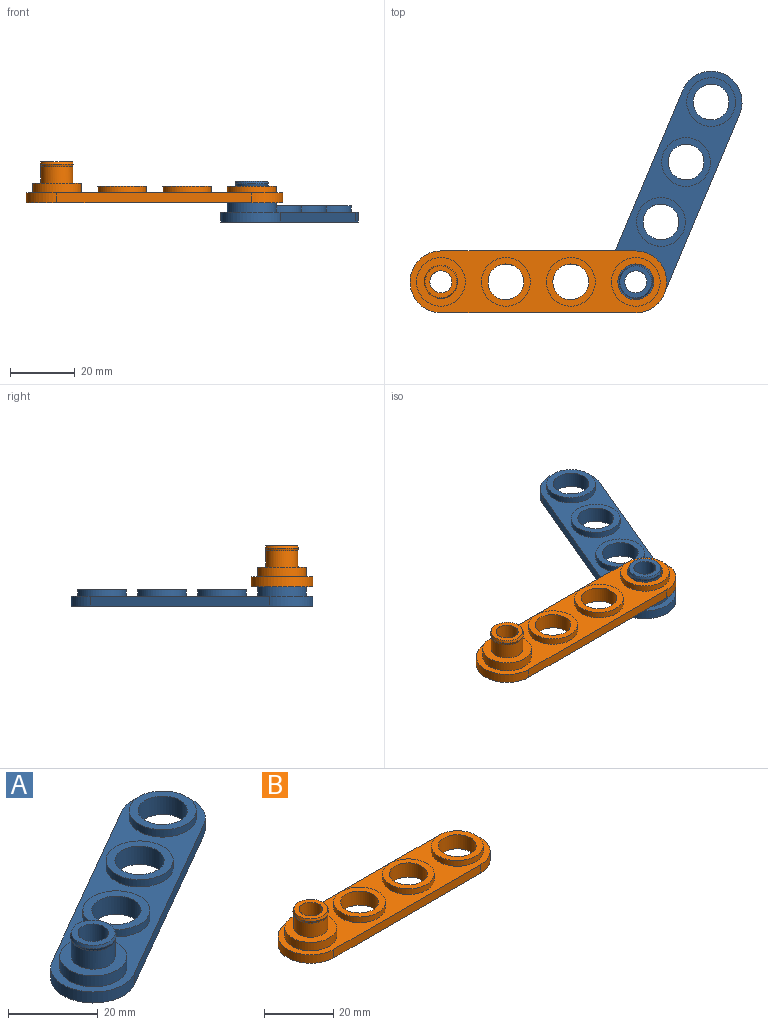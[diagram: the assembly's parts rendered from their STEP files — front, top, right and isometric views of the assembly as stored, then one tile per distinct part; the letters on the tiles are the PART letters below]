
ASSEMBLY  parts=2 mates=1
PART A: 22 faces, bbox 71x49x12.5 mm
  f0: cylinder r=9.5mm len=17.73mm, axis (0,0,-1), area 89.5mm2, adj f1,f3,f4,f5
  f1: plane 51.96x30mm, normal (0.5,-0.87,0), area 180mm2, adj f0,f2,f4,f5
  f2: cylinder r=9.5mm len=17.73mm, axis (0,0,-1), area 89.5mm2, adj f1,f3,f4,f5
  f3: plane 51.96x30mm, normal (-0.5,0.87,0), area 180mm2, adj f0,f2,f4,f5
  f4: plane 70.96x49mm, normal (0,0,1), area 716.7mm2, adj f0,f1,f2,f3,f6,f9,f12,f15
  f5: plane 70.96x49mm, normal (0,0,-1), area 1102.1mm2, adj f0,f1,f2,f3,f7,f10,f13,f18
  f6: cylinder r=7.5mm len=15mm, axis (0,0,-1), area 94.2mm2, adj f4,f8
  f7: cylinder r=5.5mm len=11mm, axis (0,0,-1), area 172.8mm2, adj f5,f8
  f8: plane 15x15mm, normal (0,0,1), area 81.7mm2, adj f6,f7
  f9: cylinder r=7.5mm len=15mm, axis (0,0,-1), area 94.2mm2, adj f4,f11
  f10: cylinder r=5.5mm len=11mm, axis (0,0,-1), area 172.8mm2, adj f5,f11
  f11: plane 15x15mm, normal (0,0,1), area 81.7mm2, adj f9,f10
  f12: cylinder r=7.5mm len=15mm, axis (0,0,-1), area 94.2mm2, adj f4,f14
  f13: cylinder r=5.5mm len=11mm, axis (0,0,-1), area 172.8mm2, adj f5,f14
  f14: plane 15x15mm, normal (0,0,1), area 81.7mm2, adj f12,f13
  f15: cylinder r=7.5mm len=15mm, axis (0,0,-1), area 141.4mm2, adj f4,f16
  f16: plane 15x15mm, normal (0,0,1), area 101.3mm2, adj f15,f17
  f17: cylinder r=4.9mm len=9.8mm, axis (0,0,-1), area 153.9mm2, adj f16,f21
  f18: cylinder r=3.4mm len=12.5mm, axis (0,0,-1), area 267mm2, adj f5,f19
  f19: plane 9.8x9.8mm, normal (0,0,1), area 39.1mm2, adj f18,f20
  f20: cone r=4.9mm half-angle=18.4deg, axis (0,0,-1), area 25mm2, adj f19,f21
  f21: cone r=5.15mm half-angle=18.4deg, axis (0,0,1), area 25mm2, adj f17,f20
PART B: 22 faces, bbox 79x19x12.5 mm
  f0: cylinder r=9.5mm len=19mm, axis (0,0,-1), area 89.5mm2, adj f1,f3,f4,f5
  f1: plane 60x3mm, normal (0,-1,0), area 180mm2, adj f0,f2,f4,f5
  f2: cylinder r=9.5mm len=19mm, axis (0,0,-1), area 89.5mm2, adj f1,f3,f4,f5
  f3: plane 60x3mm, normal (0,1,0), area 180mm2, adj f0,f2,f4,f5
  f4: plane 79x19mm, normal (0,0,1), area 716.7mm2, adj f0,f1,f2,f3,f6,f9,f12,f15
  f5: plane 79x19mm, normal (0,0,-1), area 1102.1mm2, adj f0,f1,f2,f3,f7,f10,f13,f18
  f6: cylinder r=7.5mm len=15mm, axis (0,0,-1), area 94.2mm2, adj f4,f8
  f7: cylinder r=5.5mm len=11mm, axis (0,0,-1), area 172.8mm2, adj f5,f8
  f8: plane 15x15mm, normal (0,0,1), area 81.7mm2, adj f6,f7
  f9: cylinder r=7.5mm len=15mm, axis (0,0,-1), area 94.2mm2, adj f4,f11
  f10: cylinder r=5.5mm len=11mm, axis (0,0,-1), area 172.8mm2, adj f5,f11
  f11: plane 15x15mm, normal (0,0,1), area 81.7mm2, adj f9,f10
  f12: cylinder r=7.5mm len=15mm, axis (0,0,-1), area 94.2mm2, adj f4,f14
  f13: cylinder r=5.5mm len=11mm, axis (0,0,-1), area 172.8mm2, adj f5,f14
  f14: plane 15x15mm, normal (0,0,1), area 81.7mm2, adj f12,f13
  f15: cylinder r=7.5mm len=15mm, axis (0,0,-1), area 141.4mm2, adj f4,f16
  f16: plane 15x15mm, normal (0,0,1), area 101.3mm2, adj f15,f17
  f17: cylinder r=4.9mm len=9.8mm, axis (0,0,-1), area 153.9mm2, adj f16,f21
  f18: cylinder r=3.4mm len=12.5mm, axis (0,0,-1), area 267mm2, adj f5,f19
  f19: plane 9.8x9.8mm, normal (0,0,1), area 39.1mm2, adj f18,f20
  f20: cone r=4.9mm half-angle=18.4deg, axis (0,0,-1), area 25mm2, adj f19,f21
  f21: cone r=5.15mm half-angle=18.4deg, axis (0,0,1), area 25mm2, adj f17,f20
PLACE A rot(axis=(0,0,1),37.3deg) t=(12.14,-36.73,-5.97)mm
PLACE B t=(-0.11,-0.4,-5.97)mm fixed
MATE revolute B.f2 <-> A.f0  axis (0,0,-1) through (59.89,-0.4,-5.97)mm
